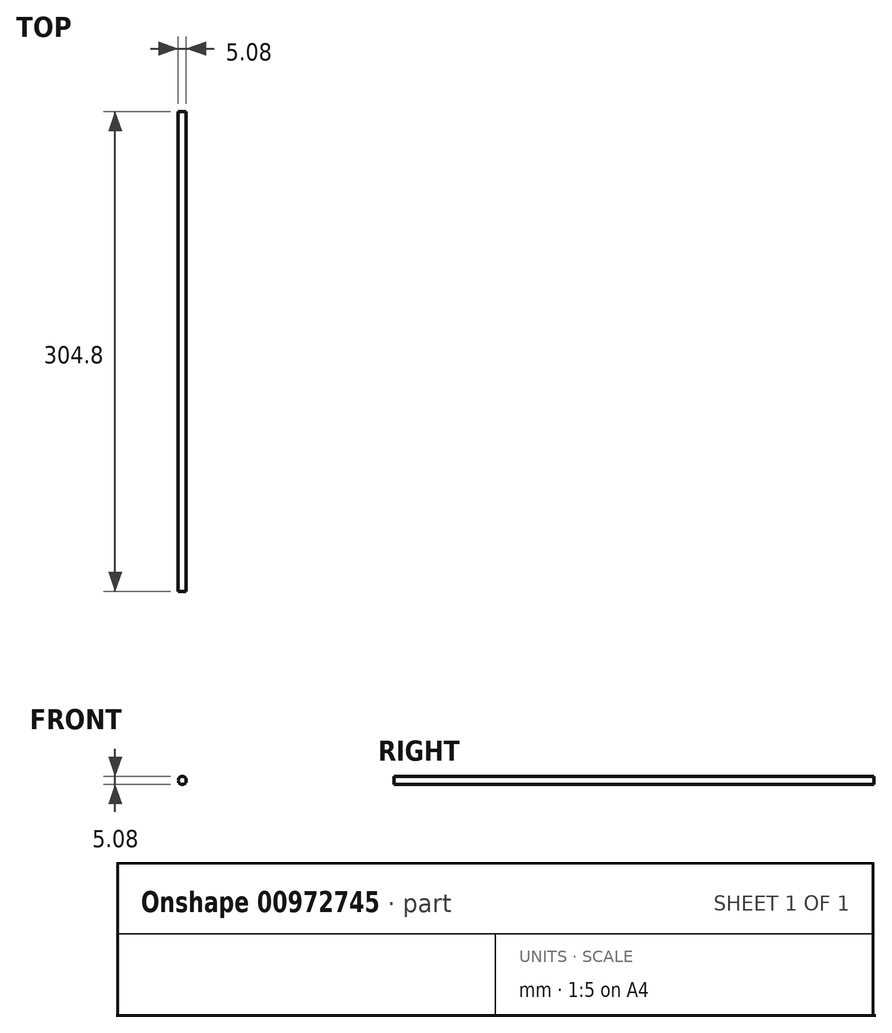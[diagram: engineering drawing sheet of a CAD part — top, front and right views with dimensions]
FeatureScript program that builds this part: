
annotation { "Feature Type Name" : "Feature", "Feature Type Description" : "" }
export const myFeature = defineFeature(function(context is Context, id is Id, definition is map)
    precondition{}
    {
        {
            var Q0;
            Q0=qCreatedBy(makeId("Front.planeOp"),FACE);
            var sketch = newSketch(context, id + "F0", { "sketchPlane" : qUnion([Q0])});
            skCircle(sketch, "E0", {"center": v(1.26, 0) * mm, "radius": 2.54 * mm});
            skSolve(sketch);
        }
        {
            var Q0;
            Q0 = qSketchRegion(id + "F0", true);
            extrude(context, id + "F1", {"entities" : qUnion([Q0]), "depth" : 304.8 * mm, "offsetDistance" : 25.4 * mm});
        }
    });
